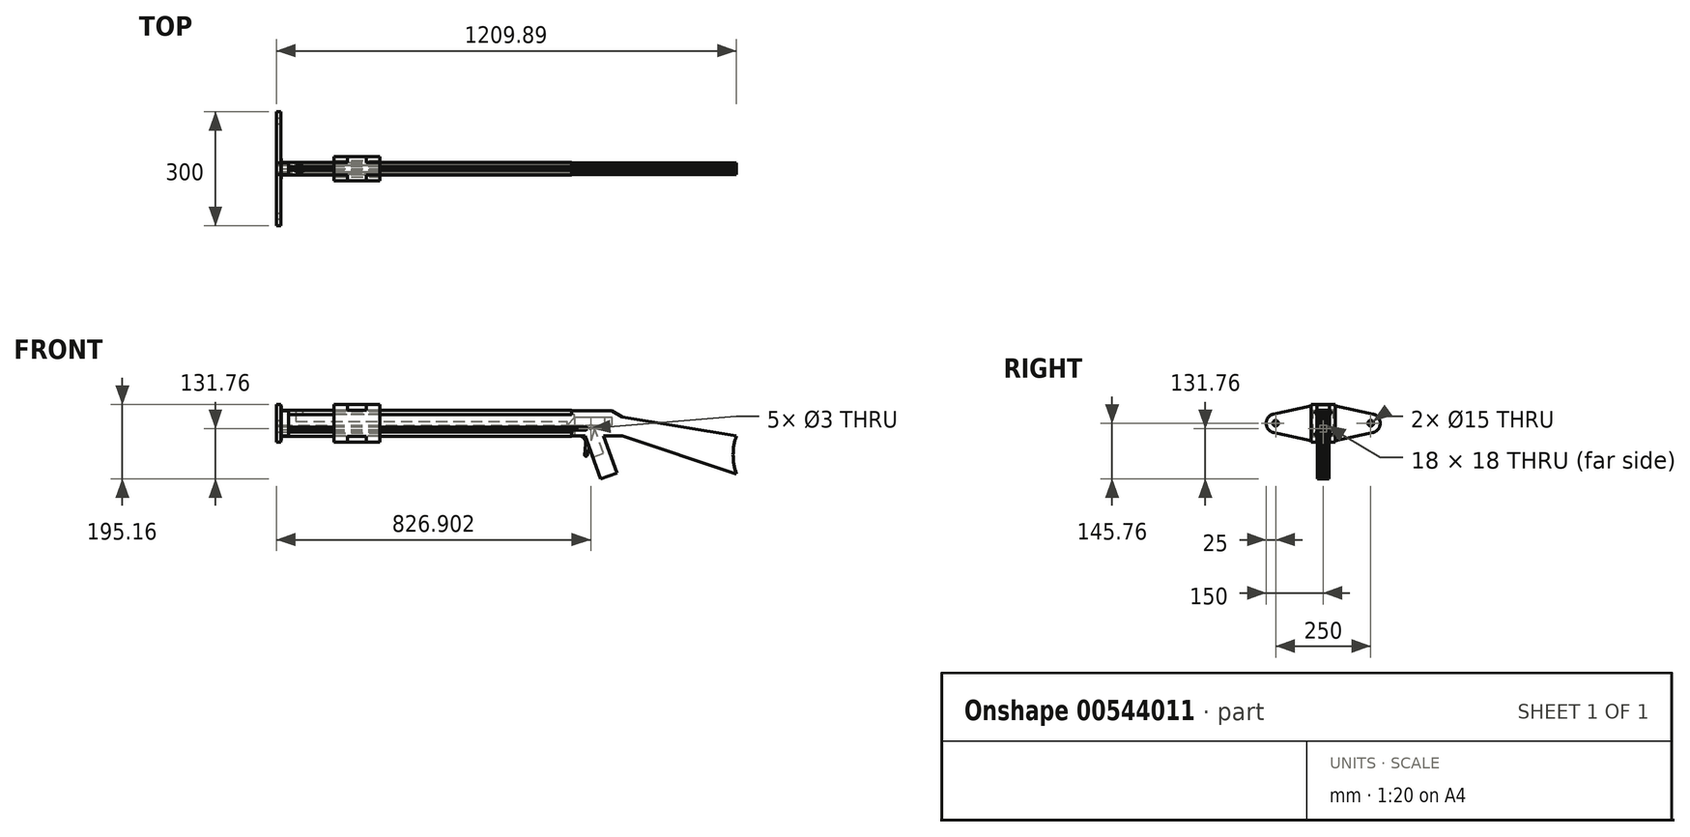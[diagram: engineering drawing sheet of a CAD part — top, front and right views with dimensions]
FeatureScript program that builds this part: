
annotation { "Feature Type Name" : "Feature", "Feature Type Description" : "" }
export const myFeature = defineFeature(function(context is Context, id is Id, definition is map)
    precondition{}
    {
        {
            var Q0;
            Q0=qCreatedBy(makeId("Front.planeOp"),FACE);
            var sketch = newSketch(context, id + "F0", { "sketchPlane" : qUnion([Q0])});
            skLineSegment(sketch, "E0", {"start": v(0, 0) * mm, "end": v(-300, 50) * mm});
            skLineSegment(sketch, "E1", {"start": v(-1197.89, 0) * mm, "end": v(-397.89, 0) * mm});
            skLineSegment(sketch, "E2", {"start": v(-397.89, 0) * mm, "end": v(-356.85, -112.76) * mm});
            skLineSegment(sketch, "E3", {"start": v(-356.85, -112.76) * mm, "end": v(-314.56, -97.37) * mm});
            skLineSegment(sketch, "E4", {"start": v(-314.56, -97.37) * mm, "end": v(-350, 0) * mm});
            skLineSegment(sketch, "E5", {"start": v(-350, 0) * mm, "end": v(-300, 0) * mm});
            skLineSegment(sketch, "E6", {"start": v(-300, 0) * mm, "end": v(0, -100) * mm});
            skLineSegment(sketch, "E7", {"start": v(-1197.89, 0) * mm, "end": v(-1197.89, 66) * mm});
            skLineSegment(sketch, "E8", {"start": v(-1197.89, 66) * mm, "end": v(-327.71, 66) * mm});
            skLineSegment(sketch, "E9", {"start": v(-300, 50) * mm, "end": v(-327.71, 66) * mm});
            skArc(sketch, "E10", {"start": v(0, 0) * mm, "mid": v(-8.58, -50) * mm, "end": v(0, -100) * mm});
            skSolve(sketch);
        }
        {
            var Q0;
            Q0=makeQuery(id+"F0.imprint","IMPRINT",FACE,{"disambiguationData":[TD([[makeQuery(id+"F0.imprint","IMPRINT",EDGE,{"derivedFrom":sQuery(id+"F0.wireOp",EDGE,"E0")}),1.0]])]});
            extrude(context, id + "F1", {"entities" : qUnion([Q0]), "depth" : 6 * mm, "offsetDistance" : 25 * mm});
        }
        {
            var Q0;
            Q0=makeQuery(id+"F1.opExtrude","CAP_FACE",FACE,{"disambiguationData":[OSD([sQuery(id+"F0.wireOp",EDGE,"E0"),sQuery(id+"F0.wireOp",EDGE,"dtHmxRtH-6a1I-GUuw-AXSh-PXiBI2h4uSGN"),sQuery(id+"F0.wireOp",EDGE,"iO8UJZjX-T8xT-28kP-745Q-Rnfn4ceRpmjQ"),sQuery(id+"F0.wireOp",EDGE,"E1"),sQuery(id+"F0.wireOp",EDGE,"E2"),sQuery(id+"F0.wireOp",EDGE,"E3"),sQuery(id+"F0.wireOp",EDGE,"E4"),sQuery(id+"F0.wireOp",EDGE,"E5"),sQuery(id+"F0.wireOp",EDGE,"E6"),sQuery(id+"F0.wireOp",EDGE,"Iz1Cz7eZ-ph4F-ZYtj-jYeC-kIhuo9vhgr1u"),sQuery(id+"F0.wireOp",EDGE,"E7"),sQuery(id+"F0.wireOp",EDGE,"E8"),sQuery(id+"F0.wireOp",EDGE,"E9")])],"isStart":false});
            var sketch = newSketch(context, id + "F2", { "sketchPlane" : qUnion([Q0])});
            skLineSegment(sketch, "E11", {"start": v(0, 0) * mm, "end": v(-300, 50) * mm});
            skLineSegment(sketch, "E12", {"start": v(-300, 50) * mm, "end": v(-327.71, 66) * mm});
            skLineSegment(sketch, "E13", {"start": v(-327.71, 66) * mm, "end": v(-1139.89, 66) * mm});
            skLineSegment(sketch, "E14", {"start": v(-1197.89, 0) * mm, "end": v(-532.89, 0) * mm});
            skLineSegment(sketch, "E15", {"start": v(-377.37, -56.38) * mm, "end": v(-356.85, -112.76) * mm});
            skLineSegment(sketch, "E16", {"start": v(-314.56, -97.37) * mm, "end": v(-350, 0) * mm});
            skLineSegment(sketch, "E17", {"start": v(-350, 0) * mm, "end": v(-300, 0) * mm});
            skLineSegment(sketch, "E18", {"start": v(-377.37, -56.38) * mm, "end": v(-349.18, -46.12) * mm});
            skLineSegment(sketch, "E19", {"start": v(-349.18, -46.12) * mm, "end": v(-376.15, 28) * mm});
            skLineSegment(sketch, "E20", {"start": v(-376.15, 28) * mm, "end": v(-326.15, 28) * mm});
            skLineSegment(sketch, "E21", {"start": v(-326.15, 28) * mm, "end": v(-326.15, 48) * mm});
            skLineSegment(sketch, "E22", {"start": v(-326.15, 48) * mm, "end": v(-426.15, 48) * mm});
            skLineSegment(sketch, "E23", {"start": v(-426.15, 48) * mm, "end": v(-426.15, 56) * mm});
            skLineSegment(sketch, "E24", {"start": v(-426.15, 56) * mm, "end": v(-1139.89, 56) * mm});
            skLineSegment(sketch, "E25", {"start": v(-1197.89, 10) * mm, "end": v(-432.89, 10) * mm});
            skLineSegment(sketch, "E26", {"start": v(-432.89, 10) * mm, "end": v(-432.89, 0) * mm});
            skLineSegment(sketch, "E27", {"start": v(-432.89, 0) * mm, "end": v(-532.89, 0) * mm});
            skLineSegment(sketch, "E28", {"start": v(-532.89, 0) * mm, "end": v(-532.89, 0) * mm});
            skLineSegment(sketch, "E29.bottom", {"start": v(-1197.89, 28) * mm, "end": v(-444.15, 28) * mm});
            skLineSegment(sketch, "E29.top", {"start": v(-1157.89, 38) * mm, "end": v(-444.15, 38) * mm});
            skLineSegment(sketch, "E29.right", {"start": v(-444.15, 28) * mm, "end": v(-444.15, 38) * mm});
            skLineSegment(sketch, "E30", {"start": v(-1197.89, 10) * mm, "end": v(-1197.89, 0) * mm});
            skLineSegment(sketch, "E31", {"start": v(-356.85, -112.76) * mm, "end": v(-314.56, -97.37) * mm});
            skLineSegment(sketch, "E32", {"start": v(-1197.89, 66) * mm, "end": v(-1197.89, 28) * mm});
            skLineSegment(sketch, "E33.right", {"start": v(-1139.89, 56) * mm, "end": v(-1139.89, 66) * mm});
            skLineSegment(sketch, "E34.trimOffspring", {"start": v(-1157.89, 66) * mm, "end": v(-1197.89, 66) * mm});
            skLineSegment(sketch, "E35", {"start": v(-1157.89, 66) * mm, "end": v(-1157.89, 38) * mm});
            skArc(sketch, "E36", {"start": v(0, 0) * mm, "mid": v(-8.58, -50) * mm, "end": v(0, -100) * mm});
            skLineSegment(sketch, "E37", {"start": v(-300, 0) * mm, "end": v(0, -100) * mm});
            skSolve(sketch);
        }
        {
            var Q0;
            Q0=makeQuery(id+"F2.imprint","IMPRINT",FACE,{"disambiguationData":[TD([[makeQuery(id+"F2.imprint","IMPRINT",EDGE,{"derivedFrom":sQuery(id+"F2.wireOp",EDGE,"E11")}),1.0]])]});
            var Q1;
            Q1=makeQuery(id+"F2.imprint","IMPRINT",FACE,{"disambiguationData":[TD([[makeQuery(id+"F2.imprint","IMPRINT",EDGE,{"derivedFrom":sQuery(id+"F2.wireOp",EDGE,"E14")}),1.0]])]});
            var Q2;
            Q2=makeQuery(id+"F2.imprint","IMPRINT",FACE,{"disambiguationData":[TD([[makeQuery(id+"F2.imprint","IMPRINT",EDGE,{"derivedFrom":sQuery(id+"F2.wireOp",EDGE,"E29.bottom")}),1.0]])]});
            extrude(context, id + "F3", {"entities" : qUnion([Q0, Q1, Q2]), "depth" : 9 * mm, "offsetDistance" : 25 * mm});
        }
        {
            var Q0;
            Q0=makeQuery(id+"F3.opExtrude","CAP_FACE",FACE,{"disambiguationData":[OSD([sQuery(id+"F2.wireOp",EDGE,"OocslNYS-gHC8-IEw6-gaO2-GtV5QujylKoG"),sQuery(id+"F2.wireOp",EDGE,"E11"),sQuery(id+"F2.wireOp",EDGE,"E12"),sQuery(id+"F2.wireOp",EDGE,"E13"),sQuery(id+"F2.wireOp",EDGE,"E15"),sQuery(id+"F2.wireOp",EDGE,"b9TXe8aB-YtLN-urND-UpbY-N42Blgdaq7uC"),sQuery(id+"F2.wireOp",EDGE,"E16"),sQuery(id+"F2.wireOp",EDGE,"E17"),sQuery(id+"F2.wireOp",EDGE,"jkZQOysl-x1w4-NRdj-YeTQ-RdmtOxi5lhvG"),sQuery(id+"F2.wireOp",EDGE,"E18"),sQuery(id+"F2.wireOp",EDGE,"E19"),sQuery(id+"F2.wireOp",EDGE,"E20"),sQuery(id+"F2.wireOp",EDGE,"E21"),sQuery(id+"F2.wireOp",EDGE,"E22"),sQuery(id+"F2.wireOp",EDGE,"E23"),sQuery(id+"F2.wireOp",EDGE,"E24"),sQuery(id+"F2.wireOp",EDGE,"VTcstgt5-tik9-lUaS-qXh4-fKFIocUgGHYO")])],"isStart":false});
            var Q1;
            Q1=makeQuery(id+"F3.opExtrude","CAP_FACE",FACE,{"disambiguationData":[OSD([sQuery(id+"F2.wireOp",EDGE,"E29.bottom"),sQuery(id+"F2.wireOp",EDGE,"E29.top"),sQuery(id+"F2.wireOp",EDGE,"E29.right"),sQuery(id+"F2.wireOp",EDGE,"3Jb5pivz-EpNF-aCuq-c8Hp-GzCfFDWtVSPK")])],"isStart":false});
            var Q2;
            Q2=makeQuery(id+"F3.opExtrude","CAP_FACE",FACE,{"disambiguationData":[OSD([sQuery(id+"F2.wireOp",EDGE,"E14"),sQuery(id+"F2.wireOp",EDGE,"E25"),sQuery(id+"F2.wireOp",EDGE,"E26"),sQuery(id+"F2.wireOp",EDGE,"E27"),sQuery(id+"F2.wireOp",EDGE,"E28"),sQuery(id+"F2.wireOp",EDGE,"E30")])],"isStart":false});
            extrude(context, id + "F4", {"entities" : qUnion([Q0, Q1, Q2]), "depth" : 9 * mm, "offsetDistance" : 25 * mm});
        }
        {
            var Q0;
            Q0=makeQuery(id+"F4.opExtrude","CAP_FACE",FACE,{"disambiguationData":[OSD([sQuery(id+"F2.wireOp",EDGE,"OocslNYS-gHC8-IEw6-gaO2-GtV5QujylKoG"),sQuery(id+"F2.wireOp",EDGE,"E11"),sQuery(id+"F2.wireOp",EDGE,"E12"),sQuery(id+"F2.wireOp",EDGE,"E13"),sQuery(id+"F2.wireOp",EDGE,"E15"),sQuery(id+"F2.wireOp",EDGE,"E16"),sQuery(id+"F2.wireOp",EDGE,"E17"),sQuery(id+"F2.wireOp",EDGE,"jkZQOysl-x1w4-NRdj-YeTQ-RdmtOxi5lhvG"),sQuery(id+"F2.wireOp",EDGE,"E18"),sQuery(id+"F2.wireOp",EDGE,"E19"),sQuery(id+"F2.wireOp",EDGE,"E20"),sQuery(id+"F2.wireOp",EDGE,"E21"),sQuery(id+"F2.wireOp",EDGE,"E22"),sQuery(id+"F2.wireOp",EDGE,"E23"),sQuery(id+"F2.wireOp",EDGE,"E24"),sQuery(id+"F2.wireOp",EDGE,"VTcstgt5-tik9-lUaS-qXh4-fKFIocUgGHYO"),sQuery(id+"F2.wireOp",EDGE,"E31")])],"isStart":false});
            var sketch = newSketch(context, id + "F5", { "sketchPlane" : qUnion([Q0])});
            skLineSegment(sketch, "E38", {"start": v(0, 0) * mm, "end": v(-300, 50) * mm});
            skLineSegment(sketch, "E39", {"start": v(-300, 50) * mm, "end": v(-327.71, 66) * mm});
            skLineSegment(sketch, "E40", {"start": v(-1197.89, 0) * mm, "end": v(-397.89, 0) * mm});
            skLineSegment(sketch, "E41", {"start": v(-397.89, 0) * mm, "end": v(-356.85, -112.76) * mm});
            skLineSegment(sketch, "E42", {"start": v(-356.85, -112.76) * mm, "end": v(-314.56, -97.37) * mm});
            skLineSegment(sketch, "E43", {"start": v(-314.56, -97.37) * mm, "end": v(-350, 0) * mm});
            skLineSegment(sketch, "E44", {"start": v(-350, 0) * mm, "end": v(-300, 0) * mm});
            skLineSegment(sketch, "E45", {"start": v(-1197.89, 0) * mm, "end": v(-1197.89, 66) * mm});
            skLineSegment(sketch, "E46", {"start": v(-1197.89, 66) * mm, "end": v(-327.71, 66) * mm});
            skArc(sketch, "E47", {"start": v(0, 0) * mm, "mid": v(-8.58, -50) * mm, "end": v(0, -100) * mm});
            skLineSegment(sketch, "E48", {"start": v(-300, 0) * mm, "end": v(0, -100) * mm});
            skSolve(sketch);
        }
        {
            var Q0;
            Q0 = qSketchRegion(id + "F5", true);
            extrude(context, id + "F6", {"entities" : qUnion([Q0]), "depth" : 6 * mm, "offsetDistance" : 25 * mm});
        }
        {
            var Q0;
            Q0=makeQuery(id+"F1.opExtrude","CAP_FACE",FACE,{"disambiguationData":[OSD([sQuery(id+"F0.wireOp",EDGE,"E0"),sQuery(id+"F0.wireOp",EDGE,"dtHmxRtH-6a1I-GUuw-AXSh-PXiBI2h4uSGN"),sQuery(id+"F0.wireOp",EDGE,"iO8UJZjX-T8xT-28kP-745Q-Rnfn4ceRpmjQ"),sQuery(id+"F0.wireOp",EDGE,"E1"),sQuery(id+"F0.wireOp",EDGE,"E2"),sQuery(id+"F0.wireOp",EDGE,"E3"),sQuery(id+"F0.wireOp",EDGE,"E4"),sQuery(id+"F0.wireOp",EDGE,"E5"),sQuery(id+"F0.wireOp",EDGE,"E6"),sQuery(id+"F0.wireOp",EDGE,"Iz1Cz7eZ-ph4F-ZYtj-jYeC-kIhuo9vhgr1u"),sQuery(id+"F0.wireOp",EDGE,"E7"),sQuery(id+"F0.wireOp",EDGE,"E8"),sQuery(id+"F0.wireOp",EDGE,"E9")])],"isStart":false});
            var sketch = newSketch(context, id + "F7", { "sketchPlane" : qUnion([Q0])});
            skLineSegment(sketch, "E49", {"start": v(-377.37, -56.38) * mm, "end": v(-349.18, -46.12) * mm});
            skLineSegment(sketch, "E50", {"start": v(-349.18, -46.12) * mm, "end": v(-376.15, 28) * mm});
            skLineSegment(sketch, "E51", {"start": v(-376.15, 28) * mm, "end": v(-326.15, 28) * mm});
            skLineSegment(sketch, "E52", {"start": v(-326.15, 28) * mm, "end": v(-326.15, 48) * mm});
            skLineSegment(sketch, "E53", {"start": v(-326.15, 48) * mm, "end": v(-426.15, 48) * mm});
            skLineSegment(sketch, "E54", {"start": v(-426.15, 48) * mm, "end": v(-426.15, 0) * mm});
            skLineSegment(sketch, "E55", {"start": v(-397.89, 0) * mm, "end": v(-377.37, -56.38) * mm});
            skLineSegment(sketch, "E56", {"start": v(-397.89, 0) * mm, "end": v(-426.15, 0) * mm});
            skSolve(sketch);
        }
        {
            var Q0;
            {var subQ0=sQuery(id+"F7.wireOp",EDGE,"E49");Q0=makeQuery(id+"F7.imprint","IMPRINT",FACE,{"disambiguationData":[TD([[makeQuery(id+"F7.imprint","IMPRINT",EDGE,{"derivedFrom":subQ0}),1.0]])]});}
            extrude(context, id + "F8", {"entities" : qUnion([Q0]), "depth" : 3 * mm, "offsetDistance" : 25 * mm});
        }
        {
            var Q0;
            Q0=makeQuery(id+"F4.opExtrude","CAP_FACE",FACE,{"disambiguationData":[OSD([sQuery(id+"F2.wireOp",EDGE,"OocslNYS-gHC8-IEw6-gaO2-GtV5QujylKoG"),sQuery(id+"F2.wireOp",EDGE,"E11"),sQuery(id+"F2.wireOp",EDGE,"E12"),sQuery(id+"F2.wireOp",EDGE,"E13"),sQuery(id+"F2.wireOp",EDGE,"E15"),sQuery(id+"F2.wireOp",EDGE,"E16"),sQuery(id+"F2.wireOp",EDGE,"E17"),sQuery(id+"F2.wireOp",EDGE,"jkZQOysl-x1w4-NRdj-YeTQ-RdmtOxi5lhvG"),sQuery(id+"F2.wireOp",EDGE,"E18"),sQuery(id+"F2.wireOp",EDGE,"E19"),sQuery(id+"F2.wireOp",EDGE,"E20"),sQuery(id+"F2.wireOp",EDGE,"E21"),sQuery(id+"F2.wireOp",EDGE,"E22"),sQuery(id+"F2.wireOp",EDGE,"E23"),sQuery(id+"F2.wireOp",EDGE,"E24"),sQuery(id+"F2.wireOp",EDGE,"VTcstgt5-tik9-lUaS-qXh4-fKFIocUgGHYO"),sQuery(id+"F2.wireOp",EDGE,"E31")])],"isStart":false});
            var sketch = newSketch(context, id + "F9", { "sketchPlane" : qUnion([Q0])});
            skLineSegment(sketch, "E57", {"start": v(-326.15, 28) * mm, "end": v(-326.15, 48) * mm});
            skLineSegment(sketch, "E58", {"start": v(-326.15, 48) * mm, "end": v(-426.15, 48) * mm});
            skLineSegment(sketch, "E59", {"start": v(-426.15, 48) * mm, "end": v(-426.15, 0) * mm});
            skLineSegment(sketch, "E60", {"start": v(-426.15, 0) * mm, "end": v(-397.89, 0) * mm});
            skLineSegment(sketch, "E61", {"start": v(-397.89, 0) * mm, "end": v(-377.37, -56.38) * mm});
            skLineSegment(sketch, "E62", {"start": v(-377.37, -56.38) * mm, "end": v(-349.18, -46.12) * mm});
            skLineSegment(sketch, "E63", {"start": v(-349.18, -46.12) * mm, "end": v(-376.15, 28) * mm});
            skLineSegment(sketch, "E64", {"start": v(-376.15, 28) * mm, "end": v(-326.15, 28) * mm});
            skSolve(sketch);
        }
        {
            var Q0;
            Q0=makeQuery(id+"F9.imprint","IMPRINT",FACE,{"disambiguationData":[TD([[makeQuery(id+"F9.imprint","IMPRINT",EDGE,{"derivedFrom":sQuery(id+"F9.wireOp",EDGE,"E57")}),1.0]])]});
            extrude(context, id + "F10", {"entities" : qUnion([Q0]), "oppositeDirection" : true, "depth" : 3 * mm, "offsetDistance" : 25 * mm});
        }
        {
            var Q0;
            Q0=makeQuery(id+"F1.opExtrude","CAP_FACE",FACE,{"disambiguationData":[OSD([sQuery(id+"F0.wireOp",EDGE,"E0"),sQuery(id+"F0.wireOp",EDGE,"dtHmxRtH-6a1I-GUuw-AXSh-PXiBI2h4uSGN"),sQuery(id+"F0.wireOp",EDGE,"iO8UJZjX-T8xT-28kP-745Q-Rnfn4ceRpmjQ"),sQuery(id+"F0.wireOp",EDGE,"E1"),sQuery(id+"F0.wireOp",EDGE,"E2"),sQuery(id+"F0.wireOp",EDGE,"E3"),sQuery(id+"F0.wireOp",EDGE,"E4"),sQuery(id+"F0.wireOp",EDGE,"E5"),sQuery(id+"F0.wireOp",EDGE,"E6"),sQuery(id+"F0.wireOp",EDGE,"Iz1Cz7eZ-ph4F-ZYtj-jYeC-kIhuo9vhgr1u"),sQuery(id+"F0.wireOp",EDGE,"E7"),sQuery(id+"F0.wireOp",EDGE,"E8"),sQuery(id+"F0.wireOp",EDGE,"E9")])],"isStart":true});
            var sketch = newSketch(context, id + "F11", { "sketchPlane" : qUnion([Q0])});
            skLineSegment(sketch, "E65.bottom", {"start": v(1197.89, 15.5) * mm, "end": v(396.15, 15.5) * mm});
            skLineSegment(sketch, "E65.top", {"start": v(1197.89, 22.5) * mm, "end": v(396.15, 22.5) * mm});
            skArc(sketch, "E66", {"start": v(396.15, 22.5) * mm, "mid": v(392.65, 19) * mm, "end": v(396.15, 15.5) * mm});
            skLineSegment(sketch, "E67", {"start": v(1197.89, 22.5) * mm, "end": v(1197.89, 15.5) * mm});
            skSolve(sketch);
        }
        {
            var Q0;
            Q0 = qSketchRegion(id + "F11", true);
            var Q1;
            Q1=makeQuery(id+"F8.opExtrude","CAP_FACE",FACE,{"disambiguationData":[OSD([sQuery(id+"F7.wireOp",EDGE,"E49"),sQuery(id+"F7.wireOp",EDGE,"E50"),sQuery(id+"F7.wireOp",EDGE,"E51"),sQuery(id+"F7.wireOp",EDGE,"E52"),sQuery(id+"F7.wireOp",EDGE,"E53"),sQuery(id+"F7.wireOp",EDGE,"E54"),sQuery(id+"F7.wireOp",EDGE,"E55"),sQuery(id+"F7.wireOp",EDGE,"E56")])],"isStart":false});
            extrude(context, id + "F12", {"entities" : qUnion([Q0]), "operationType" : NewBodyOperationType.REMOVE, "endBound" : BoundingType.THROUGH_ALL, "oppositeDirection" : true, "depth" : 25 * mm, "endBoundEntityFace" : qUnion([Q1]), "offsetDistance" : 25 * mm});
        }
        {
            var Q0;
            Q0=makeQuery(id+"F8.opExtrude","CAP_FACE",FACE,{"disambiguationData":[OSD([sQuery(id+"F7.wireOp",EDGE,"E49"),sQuery(id+"F7.wireOp",EDGE,"E50"),sQuery(id+"F7.wireOp",EDGE,"E51"),sQuery(id+"F7.wireOp",EDGE,"E52"),sQuery(id+"F7.wireOp",EDGE,"E53"),sQuery(id+"F7.wireOp",EDGE,"E54"),sQuery(id+"F7.wireOp",EDGE,"E55"),sQuery(id+"F7.wireOp",EDGE,"E56")])],"isStart":false});
            var sketch = newSketch(context, id + "F13", { "sketchPlane" : qUnion([Q0])});
            skLineSegment(sketch, "E68", {"start": v(-427.7, 14) * mm, "end": v(-411.96, 28) * mm});
            skLineSegment(sketch, "E69", {"start": v(-411.96, 28) * mm, "end": v(-401.96, 28) * mm});
            skLineSegment(sketch, "E70", {"start": v(-401.96, 28) * mm, "end": v(-401.96, 18) * mm});
            skArc(sketch, "E71", {"start": v(-374.3, 16.67) * mm, "mid": v(-381.5, 27.88) * mm, "end": v(-391.96, 19.64) * mm});
            skCircle(sketch, "E72", {"center": v(-382.99, 19) * mm, "radius": 1.5 * mm});
            skLineSegment(sketch, "E73", {"start": v(-374.3, 16.67) * mm, "end": v(-392.63, -51.78) * mm});
            skArc(sketch, "E74", {"start": v(-427.7, 14) * mm, "mid": v(-426.31, 6.84) * mm, "end": v(-423.78, 0) * mm});
            skLineSegment(sketch, "E75", {"start": v(-423.78, 0) * mm, "end": v(-415.9, 0) * mm});
            skArc(sketch, "E76", {"start": v(-398.52, -50.74) * mm, "mid": v(-396.05, -53.95) * mm, "end": v(-392.63, -51.78) * mm});
            skArc(sketch, "E77", {"start": v(-415.9, 0) * mm, "mid": v(-401.16, -6.49) * mm, "end": v(-395.98, -21.74) * mm});
            skLineSegment(sketch, "E78", {"start": v(-395.98, -21.74) * mm, "end": v(-398.52, -50.74) * mm});
            skLineSegment(sketch, "E79", {"start": v(-398.96, 15) * mm, "end": v(-396.95, 15) * mm});
            skArc(sketch, "E80", {"start": v(-396.95, 15) * mm, "mid": v(-393.55, 16.34) * mm, "end": v(-391.96, 19.64) * mm});
            skPoint(sketch, "E81.visualSharp", {"position": v(-401.96, 15) * mm});
            skArc(sketch, "E81.filletArc", {"start": v(-401.96, 18) * mm, "mid": v(-401.09, 15.88) * mm, "end": v(-398.96, 15) * mm});
            skSolve(sketch);
        }
        {
            var Q0;
            Q0 = qSketchRegion(id + "F13", true);
            extrude(context, id + "F14", {"entities" : qUnion([Q0]), "depth" : 12 * mm, "offsetDistance" : 25 * mm});
        }
        {
            var Q0;
            Q0=makeQuery(id+"F14.opExtrude","CAP_FACE",FACE,{"disambiguationData":[OSD([sQuery(id+"F13.wireOp",EDGE,"E68"),sQuery(id+"F13.wireOp",EDGE,"E69"),sQuery(id+"F13.wireOp",EDGE,"E70"),sQuery(id+"F13.wireOp",EDGE,"E71"),sQuery(id+"F13.wireOp",EDGE,"E72"),sQuery(id+"F13.wireOp",EDGE,"E73"),sQuery(id+"F13.wireOp",EDGE,"E74"),sQuery(id+"F13.wireOp",EDGE,"E75"),sQuery(id+"F13.wireOp",EDGE,"E76"),sQuery(id+"F13.wireOp",EDGE,"E77"),sQuery(id+"F13.wireOp",EDGE,"E78"),sQuery(id+"F13.wireOp",EDGE,"E79"),sQuery(id+"F13.wireOp",EDGE,"E80"),sQuery(id+"F13.wireOp",EDGE,"E81.filletArc")])],"isStart":false});
            var sketch = newSketch(context, id + "F15", { "sketchPlane" : qUnion([Q0])});
            skCircle(sketch, "E82", {"center": v(-382.99, 19) * mm, "radius": 1.5 * mm});
            skSolve(sketch);
        }
        {
            var Q0;
            Q0=makeQuery(id+"F15.imprint","IMPRINT",FACE,{"disambiguationData":[TD([[makeQuery(id+"F15.imprint","IMPRINT",EDGE,{"derivedFrom":sQuery(id+"F15.wireOp",EDGE,"E82")}),1.0]])]});
            extrude(context, id + "F16", {"entities" : qUnion([Q0]), "operationType" : NewBodyOperationType.REMOVE, "endBound" : BoundingType.SYMMETRIC, "oppositeDirection" : true, "depth" : 100 * mm, "offsetDistance" : 25 * mm});
        }
        {
            var Q0;
            {var subQ0=sQuery(id+"F7.wireOp",EDGE,"E55");var subQ2=sQuery(id+"F7.wireOp",EDGE,"E56");var subQ3=sQuery(id+"F7.wireOp",EDGE,"E54");var subQ4=sQuery(id+"F7.wireOp",EDGE,"E53");var subQ5=sQuery(id+"F7.wireOp",EDGE,"E52");var subQ6=sQuery(id+"F7.wireOp",EDGE,"E51");var subQ7=sQuery(id+"F7.wireOp",EDGE,"E50");var subQ8=sQuery(id+"F7.wireOp",EDGE,"E49");var subQ11=makeQuery(id+"F8.opExtrude","CAP_FACE",FACE,{"disambiguationData":[OSD([subQ8,subQ7,subQ6,subQ5,subQ4,subQ3,subQ0,subQ2])],"isStart":false});Q0=makeQuery(id+"F14.boolean.opBoolean","SPLIT",FACE,{"disambiguationData":[TD([makeQuery(id+"F8.opExtrude","SWEPT_FACE",FACE,{"disambiguationData":[OSD([subQ8])]})])],"derivedFrom":subQ11});}
            var sketch = newSketch(context, id + "F17", { "sketchPlane" : qUnion([Q0])});
            skLineSegment(sketch, "E83", {"start": v(-346.15, 28) * mm, "end": v(-346.15, 48) * mm});
            skLineSegment(sketch, "E84", {"start": v(-346.15, 48) * mm, "end": v(-426.15, 48) * mm});
            skLineSegment(sketch, "E85", {"start": v(-426.15, 48) * mm, "end": v(-444.15, 28) * mm});
            skLineSegment(sketch, "E86", {"start": v(-444.15, 28) * mm, "end": v(-346.15, 28) * mm});
            skSolve(sketch);
        }
        {
            var Q0;
            {var subQ1=sQuery(id+"F0.wireOp",EDGE,"E8");var subQ2=sQuery(id+"F0.wireOp",EDGE,"E7");Q0=makeQuery(id+"F12.boolean.opBoolean","SPLIT",FACE,{"disambiguationData":[TD([makeQuery(id+"F1.opExtrude","SWEPT_FACE",FACE,{"disambiguationData":[OSD([subQ1])]})])],"derivedFrom":makeQuery(id+"F1.opExtrude","SWEPT_FACE",FACE,{"disambiguationData":[OSD([subQ2])]})});}
            cPlane(context, id + "F18", {"entities" : qUnion([Q0]), "cplaneType" : CPlaneType.OFFSET, "offset" : 20 * mm, "oppositeDirection" : true, "width" : 150 * mm, "height" : 150 * mm});
        }
        {
            var Q0;
            Q0 = qSketchRegion(id + "F17", true);
            extrude(context, id + "F19", {"entities" : qUnion([Q0]), "depth" : 12 * mm, "offsetDistance" : 25 * mm});
        }
        {
            var Q0;
            Q0=qCreatedBy(id+"F18.planeOp",FACE);
            var sketch = newSketch(context, id + "F20", { "sketchPlane" : qUnion([Q0])});
            skLineSegment(sketch, "E87", {"start": v(0, 55.4) * mm, "end": v(0, 66) * mm});
            skLineSegment(sketch, "E88", {"start": v(0, 66) * mm, "end": v(10.6, 66) * mm});
            skLineSegment(sketch, "E89", {"start": v(10.6, 66) * mm, "end": v(10.6, 67.4) * mm});
            skLineSegment(sketch, "E90", {"start": v(10.6, 67.4) * mm, "end": v(-1.4, 67.4) * mm});
            skLineSegment(sketch, "E91", {"start": v(-1.4, 67.4) * mm, "end": v(-1.4, 55.4) * mm});
            skLineSegment(sketch, "E92", {"start": v(-1.4, 55.4) * mm, "end": v(0, 55.4) * mm});
            skLineSegment(sketch, "E93", {"start": v(31.4, 67.4) * mm, "end": v(31.4, 55.4) * mm});
            skLineSegment(sketch, "E94", {"start": v(31.4, 55.4) * mm, "end": v(30, 55.4) * mm});
            skLineSegment(sketch, "E95", {"start": v(30, 55.4) * mm, "end": v(30, 66) * mm});
            skLineSegment(sketch, "E96", {"start": v(30, 66) * mm, "end": v(19.4, 66) * mm});
            skLineSegment(sketch, "E97", {"start": v(19.4, 66) * mm, "end": v(19.4, 67.4) * mm});
            skLineSegment(sketch, "E98", {"start": v(19.4, 67.4) * mm, "end": v(31.4, 67.4) * mm});
            skLineSegment(sketch, "E99", {"start": v(31.4, 10.6) * mm, "end": v(31.4, -1.4) * mm});
            skLineSegment(sketch, "E100", {"start": v(31.4, -1.4) * mm, "end": v(19.4, -1.4) * mm});
            skLineSegment(sketch, "E101", {"start": v(19.4, -1.4) * mm, "end": v(19.4, 0) * mm});
            skLineSegment(sketch, "E102", {"start": v(19.4, 0) * mm, "end": v(30, 0) * mm});
            skLineSegment(sketch, "E103", {"start": v(30, 0) * mm, "end": v(30, 10.6) * mm});
            skLineSegment(sketch, "E104", {"start": v(30, 10.6) * mm, "end": v(31.4, 10.6) * mm});
            skLineSegment(sketch, "E105", {"start": v(-1.4, 10.6) * mm, "end": v(-1.4, -1.4) * mm});
            skLineSegment(sketch, "E106", {"start": v(-1.4, -1.4) * mm, "end": v(10.6, -1.4) * mm});
            skLineSegment(sketch, "E107", {"start": v(10.6, -1.4) * mm, "end": v(10.6, 0) * mm});
            skLineSegment(sketch, "E108", {"start": v(10.6, 0) * mm, "end": v(0, 0) * mm});
            skLineSegment(sketch, "E109", {"start": v(0, 0) * mm, "end": v(0, 10.6) * mm});
            skLineSegment(sketch, "E110", {"start": v(0, 10.6) * mm, "end": v(-1.4, 10.6) * mm});
            skSolve(sketch);
        }
        {
            var Q0;
            Q0=makeQuery(id+"F20.imprint","IMPRINT",FACE,{"disambiguationData":[TD([[makeQuery(id+"F20.imprint","IMPRINT",EDGE,{"derivedFrom":sQuery(id+"F20.wireOp",EDGE,"E93")}),-1.0]])]});
            var Q1;
            Q1=makeQuery(id+"F20.imprint","IMPRINT",FACE,{"disambiguationData":[TD([[makeQuery(id+"F20.imprint","IMPRINT",EDGE,{"derivedFrom":sQuery(id+"F20.wireOp",EDGE,"E87")}),1.0]])]});
            var Q2;
            Q2=makeQuery(id+"F20.imprint","IMPRINT",FACE,{"disambiguationData":[TD([[makeQuery(id+"F20.imprint","IMPRINT",EDGE,{"derivedFrom":sQuery(id+"F20.wireOp",EDGE,"E105")}),1.0]])]});
            var Q3;
            Q3=makeQuery(id+"F20.imprint","IMPRINT",FACE,{"disambiguationData":[TD([[makeQuery(id+"F20.imprint","IMPRINT",EDGE,{"derivedFrom":sQuery(id+"F20.wireOp",EDGE,"E99")}),-1.0]])]});
            var Q4;
            Q4=makeQuery(id+"F3.opExtrude","SWEPT_FACE",FACE,{"disambiguationData":[OSD([sQuery(id+"F2.wireOp",EDGE,"E26")])]});
            extrude(context, id + "F21", {"entities" : qUnion([Q0, Q1, Q2, Q3]), "endBound" : BoundingType.UP_TO_SURFACE, "oppositeDirection" : true, "depth" : 750 * mm, "endBoundEntityFace" : qUnion([Q4]), "offsetDistance" : 25 * mm});
        }
        {
            var Q0;
            Q0=makeQuery(id+"F3.opExtrude","SWEPT_FACE",FACE,{"disambiguationData":[OSD([sQuery(id+"F2.wireOp",EDGE,"E32")])]});
            cPlane(context, id + "F22", {"entities" : qUnion([Q0]), "cplaneType" : CPlaneType.OFFSET, "offset" : 0 * mm, "width" : 150 * mm, "height" : 150 * mm});
        }
        {
            var Q0;
            Q0=qCreatedBy(id+"F22.planeOp",FACE);
            var sketch = newSketch(context, id + "F23", { "sketchPlane" : qUnion([Q0])});
            skLineSegment(sketch, "E111.top", {"start": v(0, 82.4) * mm, "end": v(30, 82.4) * mm});
            skLineSegment(sketch, "E112.top", {"start": v(0, -16.4) * mm, "end": v(30, -16.4) * mm});
            skLineSegment(sketch, "E113.bottom", {"start": v(6, 10) * mm, "end": v(24, 10) * mm});
            skLineSegment(sketch, "E113.top", {"start": v(6, 28) * mm, "end": v(24, 28) * mm});
            skLineSegment(sketch, "E113.left", {"start": v(6, 10) * mm, "end": v(6, 28) * mm});
            skLineSegment(sketch, "E113.right", {"start": v(24, 10) * mm, "end": v(24, 28) * mm});
            skLineSegment(sketch, "E114", {"start": v(30, 82.4) * mm, "end": v(145.3, 57.43) * mm});
            skArc(sketch, "E115", {"start": v(145.3, 8.57) * mm, "mid": v(165, 33) * mm, "end": v(145.3, 57.43) * mm});
            skLineSegment(sketch, "E116", {"start": v(145.3, 8.57) * mm, "end": v(30, -16.4) * mm});
            skLineSegment(sketch, "E117", {"start": v(0, 82.4) * mm, "end": v(-115.3, 57.43) * mm});
            skLineSegment(sketch, "E118", {"start": v(0, -16.4) * mm, "end": v(-115.3, 8.57) * mm});
            skArc(sketch, "E119", {"start": v(-115.3, 57.43) * mm, "mid": v(-135, 33) * mm, "end": v(-115.3, 8.57) * mm});
            skCircle(sketch, "E120", {"center": v(140, 33) * mm, "radius": 7.5 * mm});
            skCircle(sketch, "E121", {"center": v(-110, 33) * mm, "radius": 7.5 * mm});
            skSolve(sketch);
        }
        {
            var Q0;
            Q0=makeQuery(id+"F23.imprint","IMPRINT",FACE,{"disambiguationData":[TD([[makeQuery(id+"F23.imprint","IMPRINT",EDGE,{"derivedFrom":sQuery(id+"F23.wireOp",EDGE,"E111.top")}),-1.0]])]});
            extrude(context, id + "F24", {"entities" : qUnion([Q0]), "depth" : 12 * mm, "offsetDistance" : 25 * mm});
        }
        {
            var Q0;
            Q0=makeQuery(id+"F6.opExtrude","CAP_FACE",FACE,{"disambiguationData":[OSD([sQuery(id+"F5.wireOp",EDGE,"E38"),sQuery(id+"F5.wireOp",EDGE,"E39"),sQuery(id+"F5.wireOp",EDGE,"E40"),sQuery(id+"F5.wireOp",EDGE,"E41"),sQuery(id+"F5.wireOp",EDGE,"E42"),sQuery(id+"F5.wireOp",EDGE,"E43"),sQuery(id+"F5.wireOp",EDGE,"ML2LZCft-hQvo-b4Ug-QH2D-hOXbCDCjm09g"),sQuery(id+"F5.wireOp",EDGE,"E44"),sQuery(id+"F5.wireOp",EDGE,"fZN8CXZm-YA8E-xqh1-GFMs-KlFaghEiiTrT"),sQuery(id+"F5.wireOp",EDGE,"E45"),sQuery(id+"F5.wireOp",EDGE,"E46")])],"isStart":false});
            var sketch = newSketch(context, id + "F25", { "sketchPlane" : qUnion([Q0])});
            skLineSegment(sketch, "E122", {"start": v(-1197.89, 78) * mm, "end": v(-1197.89, 66) * mm});
            skLineSegment(sketch, "E123", {"start": v(-1197.89, 66) * mm, "end": v(-1177.89, 66) * mm});
            skLineSegment(sketch, "E124", {"start": v(-1177.89, 66) * mm, "end": v(-1177.89, 67.4) * mm});
            skLineSegment(sketch, "E125", {"start": v(-1177.89, 67.4) * mm, "end": v(-1196.49, 67.4) * mm});
            skLineSegment(sketch, "E126", {"start": v(-1196.49, 67.4) * mm, "end": v(-1196.49, 78) * mm});
            skLineSegment(sketch, "E127", {"start": v(-1196.49, 78) * mm, "end": v(-1197.89, 78) * mm});
            skLineSegment(sketch, "E128.bottom", {"start": v(-1197.89, 0) * mm, "end": v(-1177.89, 0) * mm});
            skLineSegment(sketch, "E128.top", {"start": v(-1197.89, -12) * mm, "end": v(-1196.49, -12) * mm});
            skLineSegment(sketch, "E128.left", {"start": v(-1197.89, 0) * mm, "end": v(-1197.89, -12) * mm});
            skLineSegment(sketch, "E128.right", {"start": v(-1196.49, -1.4) * mm, "end": v(-1196.49, -12) * mm});
            skLineSegment(sketch, "E129.top", {"start": v(-1196.49, -1.4) * mm, "end": v(-1177.89, -1.4) * mm});
            skLineSegment(sketch, "E129.right", {"start": v(-1177.89, 0) * mm, "end": v(-1177.89, -1.4) * mm});
            skSolve(sketch);
        }
        {
            var Q0;
            Q0=makeQuery(id+"F25.imprint","IMPRINT",FACE,{"disambiguationData":[TD([[makeQuery(id+"F25.imprint","IMPRINT",EDGE,{"derivedFrom":sQuery(id+"F25.wireOp",EDGE,"E122")}),1.0]])]});
            var Q1;
            Q1=makeQuery(id+"F25.imprint","IMPRINT",FACE,{"disambiguationData":[TD([[makeQuery(id+"F25.imprint","IMPRINT",EDGE,{"derivedFrom":sQuery(id+"F25.wireOp",EDGE,"E128.bottom")}),-1.0]])]});
            var Q2;
            Q2=makeQuery(id+"F1.opExtrude","CAP_FACE",FACE,{"disambiguationData":[OSD([sQuery(id+"F0.wireOp",EDGE,"E0"),sQuery(id+"F0.wireOp",EDGE,"E1"),sQuery(id+"F0.wireOp",EDGE,"E2"),sQuery(id+"F0.wireOp",EDGE,"E3"),sQuery(id+"F0.wireOp",EDGE,"E4"),sQuery(id+"F0.wireOp",EDGE,"E5"),sQuery(id+"F0.wireOp",EDGE,"E6"),sQuery(id+"F0.wireOp",EDGE,"Iz1Cz7eZ-ph4F-ZYtj-jYeC-kIhuo9vhgr1u"),sQuery(id+"F0.wireOp",EDGE,"E7"),sQuery(id+"F0.wireOp",EDGE,"E8"),sQuery(id+"F0.wireOp",EDGE,"E9")])],"isStart":true});
            extrude(context, id + "F26", {"entities" : qUnion([Q0, Q1]), "endBound" : BoundingType.UP_TO_SURFACE, "oppositeDirection" : true, "depth" : 25 * mm, "endBoundEntityFace" : qUnion([Q2]), "offsetDistance" : 25 * mm});
        }
        {
            var Q0;
            Q0=makeQuery(id+"F3.opExtrude","SWEPT_FACE",FACE,{"disambiguationData":[OSD([sQuery(id+"F2.wireOp",EDGE,"E34.trimOffspring")])]});
            var sketch = newSketch(context, id + "F27", { "sketchPlane" : qUnion([Q0])});
            skLineSegment(sketch, "E130", {"start": v(-1197.89, -30) * mm, "end": v(-1177.89, -30) * mm});
            skLineSegment(sketch, "E131", {"start": v(-1177.89, -30) * mm, "end": v(-1177.89, -31.4) * mm});
            skLineSegment(sketch, "E132", {"start": v(-1177.89, -31.4) * mm, "end": v(-1196.49, -31.4) * mm});
            skLineSegment(sketch, "E133", {"start": v(-1196.49, -31.4) * mm, "end": v(-1196.49, -42) * mm});
            skLineSegment(sketch, "E134", {"start": v(-1196.49, -42) * mm, "end": v(-1197.89, -42) * mm});
            skLineSegment(sketch, "E135", {"start": v(-1197.89, -42) * mm, "end": v(-1197.89, -30) * mm});
            skLineSegment(sketch, "E136", {"start": v(-1197.89, 12) * mm, "end": v(-1197.89, 0) * mm});
            skLineSegment(sketch, "E137", {"start": v(-1197.89, 0) * mm, "end": v(-1177.89, 0) * mm});
            skLineSegment(sketch, "E138", {"start": v(-1177.89, 0) * mm, "end": v(-1177.89, 1.4) * mm});
            skLineSegment(sketch, "E139", {"start": v(-1177.89, 1.4) * mm, "end": v(-1196.49, 1.4) * mm});
            skLineSegment(sketch, "E140", {"start": v(-1196.49, 1.4) * mm, "end": v(-1196.49, 12) * mm});
            skLineSegment(sketch, "E141", {"start": v(-1196.49, 12) * mm, "end": v(-1197.89, 12) * mm});
            skSolve(sketch);
        }
        {
            var Q0;
            Q0=makeQuery(id+"F27.imprint","IMPRINT",FACE,{"disambiguationData":[TD([[makeQuery(id+"F27.imprint","IMPRINT",EDGE,{"derivedFrom":sQuery(id+"F27.wireOp",EDGE,"E136")}),1.0]])]});
            var Q1;
            Q1=makeQuery(id+"F27.imprint","IMPRINT",FACE,{"disambiguationData":[TD([[makeQuery(id+"F27.imprint","IMPRINT",EDGE,{"derivedFrom":sQuery(id+"F27.wireOp",EDGE,"E130")}),-1.0]])]});
            var Q2;
            Q2=makeQuery(id+"F4.opExtrude","SWEPT_FACE",FACE,{"disambiguationData":[OSD([sQuery(id+"F2.wireOp",EDGE,"E14"),sQuery(id+"F2.wireOp",EDGE,"E27")])]});
            extrude(context, id + "F28", {"entities" : qUnion([Q0, Q1]), "endBound" : BoundingType.UP_TO_SURFACE, "oppositeDirection" : true, "depth" : 25 * mm, "endBoundEntityFace" : qUnion([Q2]), "offsetDistance" : 25 * mm});
        }
        {
            var Q0;
            Q0=makeQuery(id+"F21.opExtrude","SWEPT_FACE",FACE,{"disambiguationData":[OSD([sQuery(id+"F20.wireOp",EDGE,"E90")])]});
            var sketch = newSketch(context, id + "F29", { "sketchPlane" : qUnion([Q0])});
            skLineSegment(sketch, "E142.bottom", {"start": v(-1157.89, -24) * mm, "end": v(-1139.89, -24) * mm});
            skLineSegment(sketch, "E142.top", {"start": v(-1157.89, -6) * mm, "end": v(-1139.89, -6) * mm});
            skLineSegment(sketch, "E142.left", {"start": v(-1157.89, -24) * mm, "end": v(-1157.89, -6) * mm});
            skLineSegment(sketch, "E142.right", {"start": v(-1139.89, -24) * mm, "end": v(-1139.89, -6) * mm});
            skSolve(sketch);
        }
        {
            var Q0;
            Q0 = qSketchRegion(id + "F29", true);
            extrude(context, id + "F30", {"entities" : qUnion([Q0]), "operationType" : NewBodyOperationType.REMOVE, "oppositeDirection" : true, "depth" : 1.5 * mm, "offsetDistance" : 25 * mm});
        }
        {
            var Q0;
            Q0=makeQuery(id+"F21.opExtrude","SWEPT_FACE",FACE,{"disambiguationData":[OSD([sQuery(id+"F20.wireOp",EDGE,"E93")])]});
            var sketch = newSketch(context, id + "F31", { "sketchPlane" : qUnion([Q0])});
            skLineSegment(sketch, "E143", {"start": v(-1057.89, -16.4) * mm, "end": v(-1022.89, -16.4) * mm});
            skLineSegment(sketch, "E144", {"start": v(-937.89, -16.4) * mm, "end": v(-937.89, 82.4) * mm});
            skLineSegment(sketch, "E145", {"start": v(-1057.89, 82.4) * mm, "end": v(-1057.89, -16.4) * mm});
            skLineSegment(sketch, "E146", {"start": v(-1057.89, 82.4) * mm, "end": v(-1022.89, 82.4) * mm});
            skLineSegment(sketch, "E147.top", {"start": v(-1022.89, 67.4) * mm, "end": v(-972.89, 67.4) * mm});
            skLineSegment(sketch, "E147.left", {"start": v(-1022.89, 82.4) * mm, "end": v(-1022.89, 67.4) * mm});
            skLineSegment(sketch, "E147.right", {"start": v(-972.89, 82.4) * mm, "end": v(-972.89, 67.4) * mm});
            skLineSegment(sketch, "E148.top", {"start": v(-1022.89, -1.4) * mm, "end": v(-972.89, -1.4) * mm});
            skLineSegment(sketch, "E148.left", {"start": v(-1022.89, -16.4) * mm, "end": v(-1022.89, -1.4) * mm});
            skLineSegment(sketch, "E148.right", {"start": v(-972.89, -16.4) * mm, "end": v(-972.89, -1.4) * mm});
            skLineSegment(sketch, "E149.trimOffspring", {"start": v(-972.89, 82.4) * mm, "end": v(-937.89, 82.4) * mm});
            skLineSegment(sketch, "E150.trimOffspring", {"start": v(-972.89, -16.4) * mm, "end": v(-937.89, -16.4) * mm});
            skSolve(sketch);
        }
        {
            var Q0;
            Q0 = qSketchRegion(id + "F31", true);
            extrude(context, id + "F32", {"entities" : qUnion([Q0]), "depth" : 15 * mm, "offsetDistance" : 25 * mm});
        }
        {
            var Q0;
            Q0=makeQuery(id+"F32.opExtrude","SWEPT_BODY",BODY,{"disambiguationData":[OSD([sQuery(id+"F31.wireOp",EDGE,"E143"),sQuery(id+"F31.wireOp",EDGE,"E144"),sQuery(id+"F31.wireOp",EDGE,"E145"),sQuery(id+"F31.wireOp",EDGE,"E146")])]});
            var Q1;
            Q1=makeQuery(id+"F3.opExtrude","CAP_FACE",FACE,{"disambiguationData":[OSD([sQuery(id+"F2.wireOp",EDGE,"OocslNYS-gHC8-IEw6-gaO2-GtV5QujylKoG"),sQuery(id+"F2.wireOp",EDGE,"E11"),sQuery(id+"F2.wireOp",EDGE,"E12"),sQuery(id+"F2.wireOp",EDGE,"E13"),sQuery(id+"F2.wireOp",EDGE,"E15"),sQuery(id+"F2.wireOp",EDGE,"E16"),sQuery(id+"F2.wireOp",EDGE,"E17"),sQuery(id+"F2.wireOp",EDGE,"jkZQOysl-x1w4-NRdj-YeTQ-RdmtOxi5lhvG"),sQuery(id+"F2.wireOp",EDGE,"E18"),sQuery(id+"F2.wireOp",EDGE,"E19"),sQuery(id+"F2.wireOp",EDGE,"E20"),sQuery(id+"F2.wireOp",EDGE,"E21"),sQuery(id+"F2.wireOp",EDGE,"E22"),sQuery(id+"F2.wireOp",EDGE,"E23"),sQuery(id+"F2.wireOp",EDGE,"E24"),sQuery(id+"F2.wireOp",EDGE,"E31"),sQuery(id+"F2.wireOp",EDGE,"E33.right")])],"isStart":false});
            mirror(context, id + "F33", {"entities" : qUnion([Q0]), "mirrorPlane" : qUnion([Q1])});
        }
        {
            var Q0;
            Q0=makeQuery(id+"F21.opExtrude","SWEPT_FACE",FACE,{"disambiguationData":[OSD([sQuery(id+"F20.wireOp",EDGE,"E90")])]});
            var sketch = newSketch(context, id + "F34", { "sketchPlane" : qUnion([Q0])});
            skLineSegment(sketch, "E151", {"start": v(-1022.89, 1.4) * mm, "end": v(-1022.89, 16.4) * mm});
            skLineSegment(sketch, "E152", {"start": v(-1022.89, 16.4) * mm, "end": v(-972.89, 16.4) * mm});
            skLineSegment(sketch, "E153", {"start": v(-972.89, 16.4) * mm, "end": v(-972.89, 1.4) * mm});
            skLineSegment(sketch, "E154", {"start": v(-972.89, 1.4) * mm, "end": v(-937.89, 1.4) * mm});
            skLineSegment(sketch, "E155", {"start": v(-937.89, 1.4) * mm, "end": v(-937.89, -31.4) * mm});
            skLineSegment(sketch, "E156", {"start": v(-937.89, -31.4) * mm, "end": v(-972.89, -31.4) * mm});
            skLineSegment(sketch, "E157", {"start": v(-972.89, -31.4) * mm, "end": v(-972.89, -46.4) * mm});
            skLineSegment(sketch, "E158", {"start": v(-972.89, -46.4) * mm, "end": v(-1022.89, -46.4) * mm});
            skLineSegment(sketch, "E159", {"start": v(-1022.89, -46.4) * mm, "end": v(-1022.89, -31.4) * mm});
            skLineSegment(sketch, "E160", {"start": v(-1022.89, -31.4) * mm, "end": v(-1057.89, -31.4) * mm});
            skLineSegment(sketch, "E161", {"start": v(-1057.89, -31.4) * mm, "end": v(-1057.89, 1.4) * mm});
            skLineSegment(sketch, "E162", {"start": v(-1057.89, 1.4) * mm, "end": v(-1022.89, 1.4) * mm});
            skSolve(sketch);
        }
        {
            var Q0;
            Q0 = qSketchRegion(id + "F34", true);
            extrude(context, id + "F35", {"entities" : qUnion([Q0]), "depth" : 15 * mm, "offsetDistance" : 25 * mm});
        }
        {
            var Q0;
            Q0=makeQuery(id+"F35.opExtrude","CAP_FACE",FACE,{"disambiguationData":[OSD([sQuery(id+"F34.wireOp",EDGE,"E151"),sQuery(id+"F34.wireOp",EDGE,"E152"),sQuery(id+"F34.wireOp",EDGE,"E153"),sQuery(id+"F34.wireOp",EDGE,"E154"),sQuery(id+"F34.wireOp",EDGE,"E155"),sQuery(id+"F34.wireOp",EDGE,"E156"),sQuery(id+"F34.wireOp",EDGE,"E157"),sQuery(id+"F34.wireOp",EDGE,"E158"),sQuery(id+"F34.wireOp",EDGE,"E159"),sQuery(id+"F34.wireOp",EDGE,"E160"),sQuery(id+"F34.wireOp",EDGE,"E161"),sQuery(id+"F34.wireOp",EDGE,"E162")])],"isStart":false});
            cPlane(context, id + "F36", {"entities" : qUnion([Q0]), "cplaneType" : CPlaneType.OFFSET, "offset" : 49.4 * mm, "oppositeDirection" : true, "width" : 150 * mm, "height" : 150 * mm});
        }
        {
            var Q0;
            Q0=makeQuery(id+"F35.opExtrude","SWEPT_BODY",BODY,{"disambiguationData":[OSD([sQuery(id+"F34.wireOp",EDGE,"E151"),sQuery(id+"F34.wireOp",EDGE,"E152"),sQuery(id+"F34.wireOp",EDGE,"E153"),sQuery(id+"F34.wireOp",EDGE,"E154"),sQuery(id+"F34.wireOp",EDGE,"E155"),sQuery(id+"F34.wireOp",EDGE,"E156"),sQuery(id+"F34.wireOp",EDGE,"E157"),sQuery(id+"F34.wireOp",EDGE,"E158"),sQuery(id+"F34.wireOp",EDGE,"E159"),sQuery(id+"F34.wireOp",EDGE,"E160"),sQuery(id+"F34.wireOp",EDGE,"E161"),sQuery(id+"F34.wireOp",EDGE,"E162")])]});
            var Q1;
            Q1=qCreatedBy(id+"F36.planeOp",FACE);
            mirror(context, id + "F37", {"entities" : qUnion([Q0]), "mirrorPlane" : qUnion([Q1])});
        }
        {
            var Q0;
            Q0=makeQuery(id+"F32.opExtrude","SWEPT_FACE",FACE,{"disambiguationData":[OSD([sQuery(id+"F31.wireOp",EDGE,"E144")])]});
            var sketch = newSketch(context, id + "F38", { "sketchPlane" : qUnion([Q0])});
            skLineSegment(sketch, "E163.bottom", {"start": v(-31.4, 64.4) * mm, "end": v(-36.4, 64.4) * mm});
            skLineSegment(sketch, "E163.top", {"start": v(-31.4, 58.4) * mm, "end": v(-36.4, 58.4) * mm});
            skLineSegment(sketch, "E163.left", {"start": v(-31.4, 64.4) * mm, "end": v(-31.4, 58.4) * mm});
            skLineSegment(sketch, "E163.right", {"start": v(-36.4, 64.4) * mm, "end": v(-36.4, 58.4) * mm});
            skLineSegment(sketch, "E164.bottom", {"start": v(-31.4, 1.6) * mm, "end": v(-36.4, 1.6) * mm});
            skLineSegment(sketch, "E164.top", {"start": v(-31.4, 7.6) * mm, "end": v(-36.4, 7.6) * mm});
            skLineSegment(sketch, "E164.left", {"start": v(-31.4, 1.6) * mm, "end": v(-31.4, 7.6) * mm});
            skLineSegment(sketch, "E164.right", {"start": v(-36.4, 1.6) * mm, "end": v(-36.4, 7.6) * mm});
            skLineSegment(sketch, "E165.bottom", {"start": v(1.4, 58.4) * mm, "end": v(6.4, 58.4) * mm});
            skLineSegment(sketch, "E165.top", {"start": v(1.4, 64.4) * mm, "end": v(6.4, 64.4) * mm});
            skLineSegment(sketch, "E165.left", {"start": v(1.4, 58.4) * mm, "end": v(1.4, 64.4) * mm});
            skLineSegment(sketch, "E165.right", {"start": v(6.4, 58.4) * mm, "end": v(6.4, 64.4) * mm});
            skLineSegment(sketch, "E166.bottom", {"start": v(1.4, 7.6) * mm, "end": v(6.4, 7.6) * mm});
            skLineSegment(sketch, "E166.top", {"start": v(1.4, 1.6) * mm, "end": v(6.4, 1.6) * mm});
            skLineSegment(sketch, "E166.left", {"start": v(1.4, 7.6) * mm, "end": v(1.4, 1.6) * mm});
            skLineSegment(sketch, "E166.right", {"start": v(6.4, 7.6) * mm, "end": v(6.4, 1.6) * mm});
            skSolve(sketch);
        }
        {
            var Q0;
            Q0=makeQuery(id+"F38.imprint","IMPRINT",FACE,{"disambiguationData":[TD([[makeQuery(id+"F38.imprint","IMPRINT",EDGE,{"derivedFrom":sQuery(id+"F38.wireOp",EDGE,"E164.bottom")}),-1.0]])]});
            var Q1;
            Q1=makeQuery(id+"F38.imprint","IMPRINT",FACE,{"disambiguationData":[TD([[makeQuery(id+"F38.imprint","IMPRINT",EDGE,{"derivedFrom":sQuery(id+"F38.wireOp",EDGE,"E166.bottom")}),-1.0]])]});
            var Q2;
            Q2=makeQuery(id+"F38.imprint","IMPRINT",FACE,{"disambiguationData":[TD([[makeQuery(id+"F38.imprint","IMPRINT",EDGE,{"derivedFrom":sQuery(id+"F38.wireOp",EDGE,"E163.bottom")}),1.0]])]});
            var Q3;
            Q3=makeQuery(id+"F38.imprint","IMPRINT",FACE,{"disambiguationData":[TD([[makeQuery(id+"F38.imprint","IMPRINT",EDGE,{"derivedFrom":sQuery(id+"F38.wireOp",EDGE,"E165.bottom")}),1.0]])]});
            extrude(context, id + "F39", {"entities" : qUnion([Q0, Q1, Q2, Q3]), "operationType" : NewBodyOperationType.REMOVE, "endBound" : BoundingType.UP_TO_NEXT, "oppositeDirection" : true, "depth" : 25 * mm, "offsetDistance" : 25 * mm});
        }
    });
